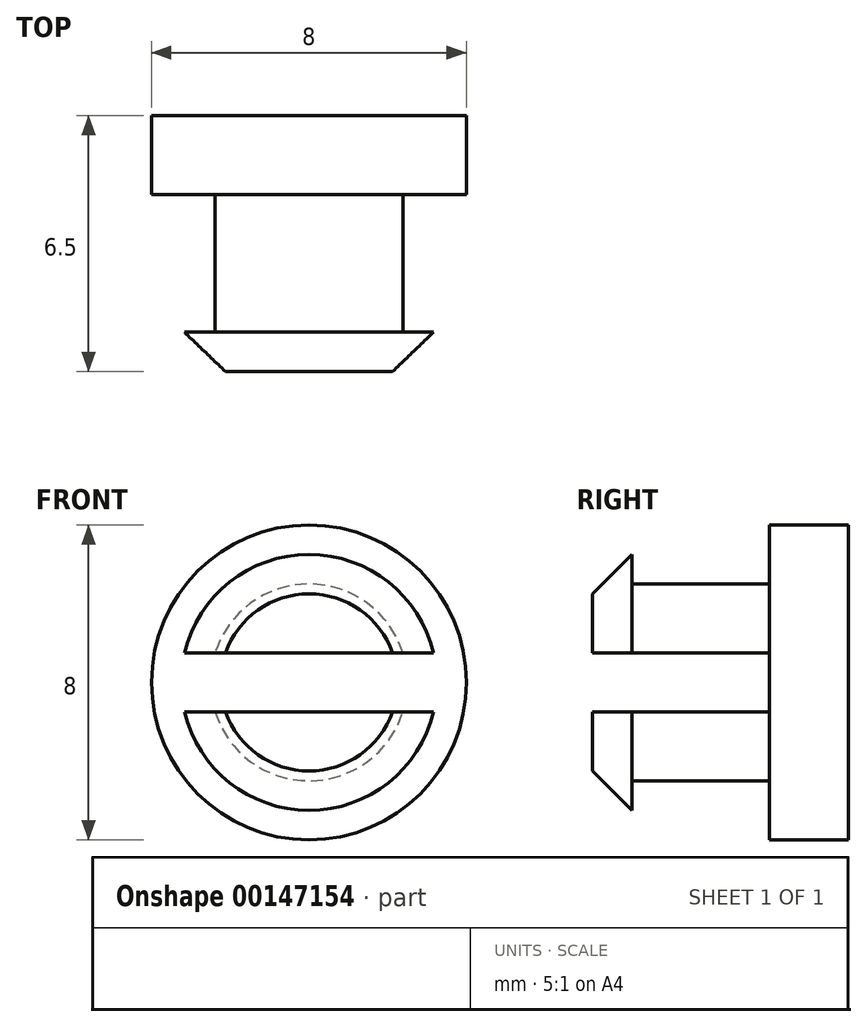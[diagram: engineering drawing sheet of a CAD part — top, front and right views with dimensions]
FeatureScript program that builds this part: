
annotation { "Feature Type Name" : "Feature", "Feature Type Description" : "" }
export const myFeature = defineFeature(function(context is Context, id is Id, definition is map)
    precondition{}
    {
        {
            var Q0;
            Q0=qCreatedBy(makeId("Front.planeOp"),FACE);
            var sketch = newSketch(context, id + "F0", { "sketchPlane" : qUnion([Q0])});
            skCircle(sketch, "E0", {"center": v(0, 0) * mm, "radius": 4 * mm});
            skCircle(sketch, "E1", {"center": v(0, 0) * mm, "radius": 2.5 * mm});
            skLineSegment(sketch, "E2.bottom", {"start": v(-3.5, 0.75) * mm, "end": v(3.5, 0.75) * mm});
            skLineSegment(sketch, "E2.top", {"start": v(-3.5, -0.75) * mm, "end": v(3.5, -0.75) * mm});
            skLineSegment(sketch, "E2.left", {"start": v(-3.5, 0.75) * mm, "end": v(-3.5, -0.75) * mm});
            skLineSegment(sketch, "E2.right", {"start": v(3.5, 0.75) * mm, "end": v(3.5, -0.75) * mm});
            skCircle(sketch, "E3", {"center": v(0, 0) * mm, "radius": 3.25 * mm});
            skSolve(sketch);
        }
        {
            var Q0;
            {var subQ0=sQuery(id+"F0.wireOp",EDGE,"E2.bottom");var subQ1=sQuery(id+"F0.wireOp",EDGE,"E1");var subQ2=makeQuery(id+"F0.imprint","INTERSECT",VERTEX,{"disambiguationData":[OD(0.0)],"derivedFrom":[subQ1,subQ0]});Q0=makeQuery(id+"F0.imprint","IMPRINT",FACE,{"disambiguationData":[TD([[makeQuery(id+"F0.imprint","IMPRINT",EDGE,{"disambiguationData":[TD([[subQ2,-1.0]])],"derivedFrom":subQ1}),1.0]])]});}
            var Q1;
            {var subQ5=sQuery(id+"F0.wireOp",EDGE,"E2.right");Q1=makeQuery(id+"F0.imprint","IMPRINT",FACE,{"disambiguationData":[TD([[makeQuery(id+"F0.imprint","IMPRINT",EDGE,{"derivedFrom":subQ5}),-1.0]])]});}
            var Q2;
            {var subQ5=sQuery(id+"F0.wireOp",EDGE,"E2.left");Q2=makeQuery(id+"F0.imprint","IMPRINT",FACE,{"disambiguationData":[TD([[makeQuery(id+"F0.imprint","IMPRINT",EDGE,{"derivedFrom":subQ5}),1.0]])]});}
            var Q3;
            {var subQ0=sQuery(id+"F0.wireOp",EDGE,"E2.top");var subQ1=sQuery(id+"F0.wireOp",EDGE,"E1");var subQ2=makeQuery(id+"F0.imprint","INTERSECT",VERTEX,{"disambiguationData":[OD(0.0)],"derivedFrom":[subQ1,subQ0]});Q3=makeQuery(id+"F0.imprint","IMPRINT",FACE,{"disambiguationData":[TD([[makeQuery(id+"F0.imprint","IMPRINT",EDGE,{"disambiguationData":[TD([[subQ2,-1.0]])],"derivedFrom":subQ1}),1.0]])]});}
            var Q4;
            Q4=makeQuery(id+"F0.imprint","IMPRINT",FACE,{"disambiguationData":[TD([[makeQuery(id+"F0.imprint","IMPRINT",EDGE,{"derivedFrom":sQuery(id+"F0.wireOp",EDGE,"E0")}),1.0]])]});
            var Q5;
            {var subQ0=sQuery(id+"F0.wireOp",EDGE,"E2.bottom");var subQ1=sQuery(id+"F0.wireOp",EDGE,"E1");var subQ2=makeQuery(id+"F0.imprint","INTERSECT",VERTEX,{"disambiguationData":[OD(0.0)],"derivedFrom":[subQ1,subQ0]});Q5=makeQuery(id+"F0.imprint","IMPRINT",FACE,{"disambiguationData":[TD([[makeQuery(id+"F0.imprint","IMPRINT",EDGE,{"disambiguationData":[TD([[subQ2,1.0]])],"derivedFrom":subQ1}),1.0]])]});}
            var Q6;
            {var subQ1=sQuery(id+"F0.wireOp",EDGE,"E1");var subQ5=sQuery(id+"F0.wireOp",EDGE,"E2.bottom");var subQ8=makeQuery(id+"F0.imprint","INTERSECT",VERTEX,{"disambiguationData":[OD(0.0)],"derivedFrom":[subQ1,subQ5]});Q6=makeQuery(id+"F0.imprint","IMPRINT",FACE,{"disambiguationData":[TD([[makeQuery(id+"F0.imprint","IMPRINT",EDGE,{"disambiguationData":[TD([[subQ8,-1.0]])],"derivedFrom":subQ1}),-1.0]])]});}
            var Q7;
            {var subQ0=sQuery(id+"F0.wireOp",EDGE,"E2.top");var subQ1=sQuery(id+"F0.wireOp",EDGE,"E1");var subQ2=makeQuery(id+"F0.imprint","INTERSECT",VERTEX,{"disambiguationData":[OD(0.0)],"derivedFrom":[subQ1,subQ0]});Q7=makeQuery(id+"F0.imprint","IMPRINT",FACE,{"disambiguationData":[TD([[makeQuery(id+"F0.imprint","IMPRINT",EDGE,{"disambiguationData":[TD([[subQ2,-1.0]])],"derivedFrom":subQ1}),-1.0]])]});}
            var Q8;
            {var subQ1=sQuery(id+"F0.wireOp",EDGE,"E1");var subQ6=sQuery(id+"F0.wireOp",EDGE,"E2.bottom");var subQ7=makeQuery(id+"F0.imprint","INTERSECT",VERTEX,{"disambiguationData":[OD(1.0)],"derivedFrom":[subQ1,subQ6]});Q8=makeQuery(id+"F0.imprint","IMPRINT",FACE,{"disambiguationData":[TD([[makeQuery(id+"F0.imprint","IMPRINT",EDGE,{"disambiguationData":[TD([[subQ7,1.0]])],"derivedFrom":subQ1}),-1.0]])]});}
            var Q9;
            {var subQ0=sQuery(id+"F0.wireOp",EDGE,"E2.bottom");var subQ1=sQuery(id+"F0.wireOp",EDGE,"E1");var subQ2=makeQuery(id+"F0.imprint","INTERSECT",VERTEX,{"disambiguationData":[OD(0.0)],"derivedFrom":[subQ1,subQ0]});Q9=makeQuery(id+"F0.imprint","IMPRINT",FACE,{"disambiguationData":[TD([[makeQuery(id+"F0.imprint","IMPRINT",EDGE,{"disambiguationData":[TD([[subQ2,1.0]])],"derivedFrom":subQ1}),-1.0]])]});}
            extrude(context, id + "F1", {"entities" : qUnion([Q0, Q1, Q2, Q3, Q4, Q5, Q6, Q7, Q8, Q9]), "depth" : 2 * mm});
        }
        {
            var Q0;
            {var subQ0=sQuery(id+"F0.wireOp",EDGE,"E2.bottom");var subQ1=sQuery(id+"F0.wireOp",EDGE,"E1");var subQ2=makeQuery(id+"F0.imprint","INTERSECT",VERTEX,{"disambiguationData":[OD(0.0)],"derivedFrom":[subQ1,subQ0]});Q0=makeQuery(id+"F0.imprint","IMPRINT",FACE,{"disambiguationData":[TD([[makeQuery(id+"F0.imprint","IMPRINT",EDGE,{"disambiguationData":[TD([[subQ2,1.0]])],"derivedFrom":subQ1}),1.0]])]});}
            var Q1;
            {var subQ0=sQuery(id+"F0.wireOp",EDGE,"E2.top");var subQ1=sQuery(id+"F0.wireOp",EDGE,"E1");var subQ2=makeQuery(id+"F0.imprint","INTERSECT",VERTEX,{"disambiguationData":[OD(0.0)],"derivedFrom":[subQ1,subQ0]});Q1=makeQuery(id+"F0.imprint","IMPRINT",FACE,{"disambiguationData":[TD([[makeQuery(id+"F0.imprint","IMPRINT",EDGE,{"disambiguationData":[TD([[subQ2,-1.0]])],"derivedFrom":subQ1}),1.0]])]});}
            extrude(context, id + "F2", {"entities" : qUnion([Q0, Q1]), "operationType" : NewBodyOperationType.ADD, "depth" : 5.5 * mm});
        }
        {
            var Q0;
            {var subQ0=sQuery(id+"F0.wireOp",EDGE,"E2.top");var subQ1=sQuery(id+"F0.wireOp",EDGE,"E1");var subQ2=makeQuery(id+"F0.imprint","INTERSECT",VERTEX,{"disambiguationData":[OD(0.0)],"derivedFrom":[subQ1,subQ0]});Q0=makeQuery(id+"F0.imprint","IMPRINT",FACE,{"disambiguationData":[TD([[makeQuery(id+"F0.imprint","IMPRINT",EDGE,{"disambiguationData":[TD([[subQ2,-1.0]])],"derivedFrom":subQ1}),-1.0]])]});}
            var Q1;
            {var subQ0=sQuery(id+"F0.wireOp",EDGE,"E2.bottom");var subQ1=sQuery(id+"F0.wireOp",EDGE,"E1");var subQ2=makeQuery(id+"F0.imprint","INTERSECT",VERTEX,{"disambiguationData":[OD(0.0)],"derivedFrom":[subQ1,subQ0]});Q1=makeQuery(id+"F0.imprint","IMPRINT",FACE,{"disambiguationData":[TD([[makeQuery(id+"F0.imprint","IMPRINT",EDGE,{"disambiguationData":[TD([[subQ2,1.0]])],"derivedFrom":subQ1}),-1.0]])]});}
            var Q2;
            {var subQ0=sQuery(id+"F0.wireOp",EDGE,"E2.bottom");var subQ1=sQuery(id+"F0.wireOp",EDGE,"E1");var subQ2=makeQuery(id+"F0.imprint","INTERSECT",VERTEX,{"disambiguationData":[OD(0.0)],"derivedFrom":[subQ1,subQ0]});Q2=makeQuery(id+"F0.imprint","IMPRINT",FACE,{"disambiguationData":[TD([[makeQuery(id+"F0.imprint","IMPRINT",EDGE,{"disambiguationData":[TD([[subQ2,1.0]])],"derivedFrom":subQ1}),1.0]])]});}
            var Q3;
            {var subQ0=sQuery(id+"F0.wireOp",EDGE,"E2.top");var subQ1=sQuery(id+"F0.wireOp",EDGE,"E1");var subQ2=makeQuery(id+"F0.imprint","INTERSECT",VERTEX,{"disambiguationData":[OD(0.0)],"derivedFrom":[subQ1,subQ0]});Q3=makeQuery(id+"F0.imprint","IMPRINT",FACE,{"disambiguationData":[TD([[makeQuery(id+"F0.imprint","IMPRINT",EDGE,{"disambiguationData":[TD([[subQ2,-1.0]])],"derivedFrom":subQ1}),1.0]])]});}
            extrude(context, id + "F3", {"entities" : qUnion([Q0, Q1, Q2, Q3]), "operationType" : NewBodyOperationType.ADD, "depth" : 6.5 * mm, "hasSecondDirection" : true, "secondDirectionOppositeDirection" : false, "secondDirectionDepth" : 5.5 * mm});
        }
        {
            var Q0;
            {var subQ0=sQuery(id+"F0.wireOp",EDGE,"E3");var subQ1=sQuery(id+"F0.wireOp",EDGE,"E2.bottom");Q0=makeQuery(id+"F3.opExtrude","CAP_EDGE",EDGE,{"disambiguationData":[OSD([subQ0]),TDD([makeQuery(id+"F0.imprint","IMPRINT",EDGE,{"disambiguationData":[TD([[makeQuery(id+"F0.imprint","INTERSECT",VERTEX,{"disambiguationData":[OD(0.0)],"derivedFrom":[subQ1,subQ0]}),1.0]])],"derivedFrom":subQ0})])],"isStart":false});}
            var Q1;
            {var subQ0=sQuery(id+"F0.wireOp",EDGE,"E3");var subQ1=sQuery(id+"F0.wireOp",EDGE,"E2.top");Q1=makeQuery(id+"F3.opExtrude","CAP_EDGE",EDGE,{"disambiguationData":[OSD([subQ0]),TDD([makeQuery(id+"F0.imprint","IMPRINT",EDGE,{"disambiguationData":[TD([[makeQuery(id+"F0.imprint","INTERSECT",VERTEX,{"disambiguationData":[OD(0.0)],"derivedFrom":[subQ1,subQ0]}),-1.0]])],"derivedFrom":subQ0})])],"isStart":false});}
            chamfer(context, id + "F4", {"entities" : qUnion([Q0, Q1]), "width" : 1 * mm, "tangentPropagation" : true});
        }
    });
